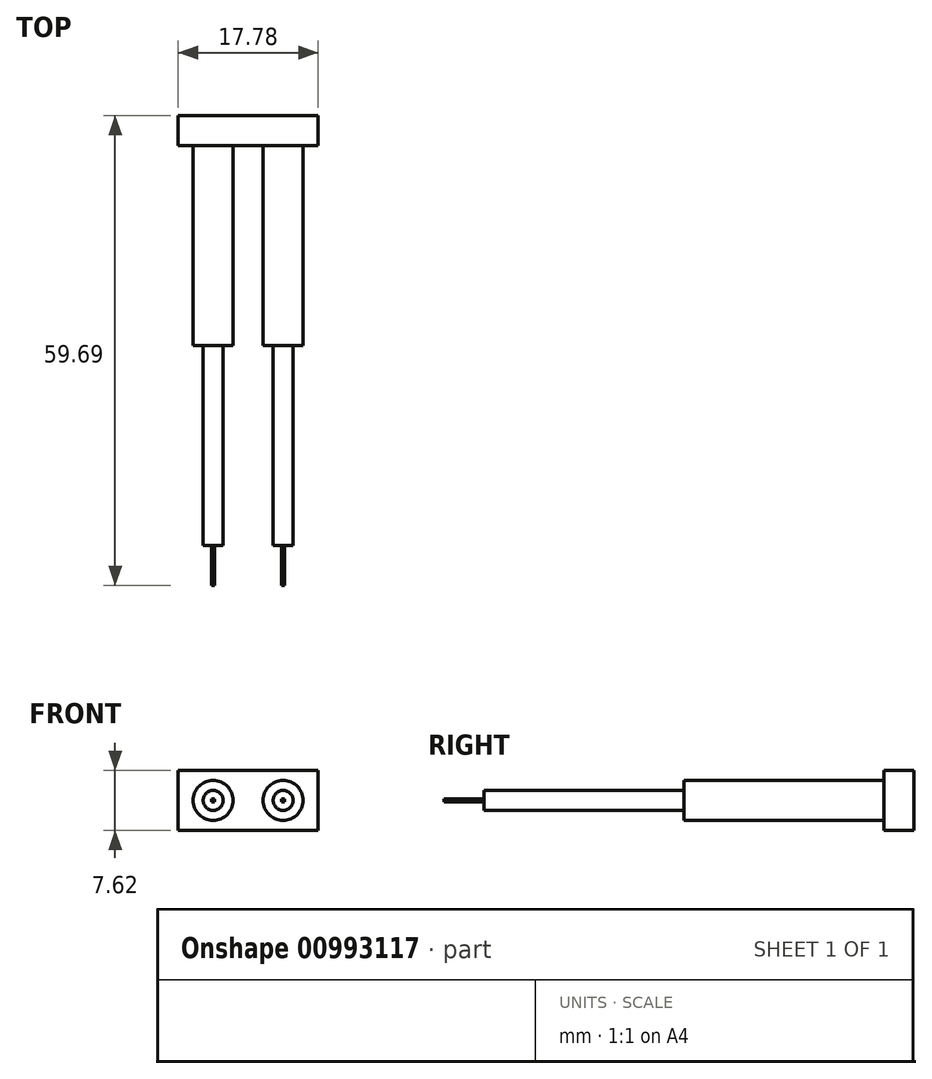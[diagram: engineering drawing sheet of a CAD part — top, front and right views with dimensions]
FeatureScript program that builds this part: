
annotation { "Feature Type Name" : "Feature", "Feature Type Description" : "" }
export const myFeature = defineFeature(function(context is Context, id is Id, definition is map)
    precondition{}
    {
        {
            var Q0;
            Q0=qCreatedBy(makeId("Front.planeOp"),FACE);
            var sketch = newSketch(context, id + "F0", { "sketchPlane" : qUnion([Q0])});
            skLineSegment(sketch, "E0.bottom", {"start": v(-44.42, 27.4) * mm, "end": v(-26.64, 27.4) * mm});
            skLineSegment(sketch, "E0.top", {"start": v(-44.42, 19.79) * mm, "end": v(-26.64, 19.79) * mm});
            skLineSegment(sketch, "E0.left", {"start": v(-44.42, 27.4) * mm, "end": v(-44.42, 19.79) * mm});
            skLineSegment(sketch, "E0.right", {"start": v(-26.64, 27.4) * mm, "end": v(-26.64, 19.79) * mm});
            skCircle(sketch, "E1", {"center": v(-39.97, 23.6) * mm, "radius": 2.54 * mm});
            skPoint(sketch, "E1.centerSnap0", {"position": v(-44.42, 23.6) * mm});
            skCircle(sketch, "E2", {"center": v(-39.97, 23.6) * mm, "radius": 1.27 * mm});
            skCircle(sketch, "E3", {"center": v(-31.08, 23.6) * mm, "radius": 2.54 * mm});
            skCircle(sketch, "E4", {"center": v(-31.08, 23.6) * mm, "radius": 1.27 * mm});
            skSolve(sketch);
        }
        {
            var Q0;
            Q0=makeQuery(id+"F0.imprint","IMPRINT",FACE,{"disambiguationData":[TD([[makeQuery(id+"F0.imprint","IMPRINT",EDGE,{"derivedFrom":sQuery(id+"F0.wireOp",EDGE,"E0.bottom")}),-1.0]])]});
            var Q1;
            Q1=makeQuery(id+"F0.imprint","IMPRINT",FACE,{"disambiguationData":[TD([[makeQuery(id+"F0.imprint","IMPRINT",EDGE,{"derivedFrom":sQuery(id+"F0.wireOp",EDGE,"E1")}),1.0]])]});
            var Q2;
            Q2=makeQuery(id+"F0.imprint","IMPRINT",FACE,{"disambiguationData":[TD([[makeQuery(id+"F0.imprint","IMPRINT",EDGE,{"derivedFrom":sQuery(id+"F0.wireOp",EDGE,"E2")}),1.0]])]});
            var Q3;
            Q3=makeQuery(id+"F0.imprint","IMPRINT",FACE,{"disambiguationData":[TD([[makeQuery(id+"F0.imprint","IMPRINT",EDGE,{"derivedFrom":sQuery(id+"F0.wireOp",EDGE,"E3")}),1.0]])]});
            var Q4;
            Q4=makeQuery(id+"F0.imprint","IMPRINT",FACE,{"disambiguationData":[TD([[makeQuery(id+"F0.imprint","IMPRINT",EDGE,{"derivedFrom":sQuery(id+"F0.wireOp",EDGE,"E4")}),1.0]])]});
            extrude(context, id + "F1", {"entities" : qUnion([Q0, Q1, Q2, Q3, Q4]), "oppositeDirection" : true, "depth" : 3.8 * mm, "offsetDistance" : 25.4 * mm});
        }
        {
            var Q0;
            Q0=makeQuery(id+"F0.imprint","IMPRINT",FACE,{"disambiguationData":[TD([[makeQuery(id+"F0.imprint","IMPRINT",EDGE,{"derivedFrom":sQuery(id+"F0.wireOp",EDGE,"E2")}),1.0]])]});
            var Q1;
            Q1=makeQuery(id+"F0.imprint","IMPRINT",FACE,{"disambiguationData":[TD([[makeQuery(id+"F0.imprint","IMPRINT",EDGE,{"derivedFrom":sQuery(id+"F0.wireOp",EDGE,"E4")}),1.0]])]});
            extrude(context, id + "F2", {"entities" : qUnion([Q0, Q1]), "operationType" : NewBodyOperationType.ADD, "depth" : 50.8 * mm, "offsetDistance" : 25.4 * mm});
        }
        {
            var Q0;
            Q0=makeQuery(id+"F0.imprint","IMPRINT",FACE,{"disambiguationData":[TD([[makeQuery(id+"F0.imprint","IMPRINT",EDGE,{"derivedFrom":sQuery(id+"F0.wireOp",EDGE,"E1")}),1.0]])]});
            var Q1;
            Q1=makeQuery(id+"F0.imprint","IMPRINT",FACE,{"disambiguationData":[TD([[makeQuery(id+"F0.imprint","IMPRINT",EDGE,{"derivedFrom":sQuery(id+"F0.wireOp",EDGE,"E3")}),1.0]])]});
            extrude(context, id + "F3", {"entities" : qUnion([Q0, Q1]), "operationType" : NewBodyOperationType.ADD, "depth" : 25.4 * mm, "offsetDistance" : 25.4 * mm});
        }
        {
            var Q0;
            Q0=makeQuery(id+"F2.opExtrude","CAP_FACE",FACE,{"disambiguationData":[OSD([sQuery(id+"F0.wireOp",EDGE,"E2")])],"isStart":false});
            var sketch = newSketch(context, id + "F4", { "sketchPlane" : qUnion([Q0])});
            skLineSegment(sketch, "E5.bottom", {"start": v(-39.8, 23.78) * mm, "end": v(-40.16, 23.78) * mm});
            skLineSegment(sketch, "E5.top", {"start": v(-39.8, 23.42) * mm, "end": v(-40.16, 23.42) * mm});
            skLineSegment(sketch, "E5.left", {"start": v(-39.8, 23.78) * mm, "end": v(-39.8, 23.42) * mm});
            skLineSegment(sketch, "E5.right", {"start": v(-40.16, 23.78) * mm, "end": v(-40.16, 23.42) * mm});
            skPoint(sketch, "E5.middle", {"position": v(-39.97, 23.6) * mm});
            skSolve(sketch);
        }
        {
            var Q0;
            Q0=makeQuery(id+"F4.imprint","IMPRINT",FACE,{"disambiguationData":[TD([[makeQuery(id+"F4.imprint","IMPRINT",EDGE,{"derivedFrom":sQuery(id+"F4.wireOp",EDGE,"E5.bottom")}),1.0]])]});
            extrude(context, id + "F5", {"entities" : qUnion([Q0]), "operationType" : NewBodyOperationType.ADD, "depth" : 5.08 * mm, "offsetDistance" : 25.4 * mm});
        }
        {
            var Q0;
            Q0=makeQuery(id+"F2.opExtrude","CAP_FACE",FACE,{"disambiguationData":[OSD([sQuery(id+"F0.wireOp",EDGE,"E4")])],"isStart":false});
            var sketch = newSketch(context, id + "F6", { "sketchPlane" : qUnion([Q0])});
            skLineSegment(sketch, "E6.bottom", {"start": v(-30.9, 23.79) * mm, "end": v(-31.27, 23.79) * mm});
            skLineSegment(sketch, "E6.top", {"start": v(-30.9, 23.41) * mm, "end": v(-31.27, 23.41) * mm});
            skLineSegment(sketch, "E6.left", {"start": v(-30.9, 23.79) * mm, "end": v(-30.9, 23.41) * mm});
            skLineSegment(sketch, "E6.right", {"start": v(-31.27, 23.79) * mm, "end": v(-31.27, 23.41) * mm});
            skPoint(sketch, "E6.middle", {"position": v(-31.08, 23.6) * mm});
            skSolve(sketch);
        }
        {
            var Q0;
            Q0=makeQuery(id+"F6.imprint","IMPRINT",FACE,{"disambiguationData":[TD([[makeQuery(id+"F6.imprint","IMPRINT",EDGE,{"derivedFrom":sQuery(id+"F6.wireOp",EDGE,"E6.bottom")}),1.0]])]});
            extrude(context, id + "F7", {"entities" : qUnion([Q0]), "operationType" : NewBodyOperationType.ADD, "depth" : 5.08 * mm, "offsetDistance" : 25.4 * mm});
        }
    });
